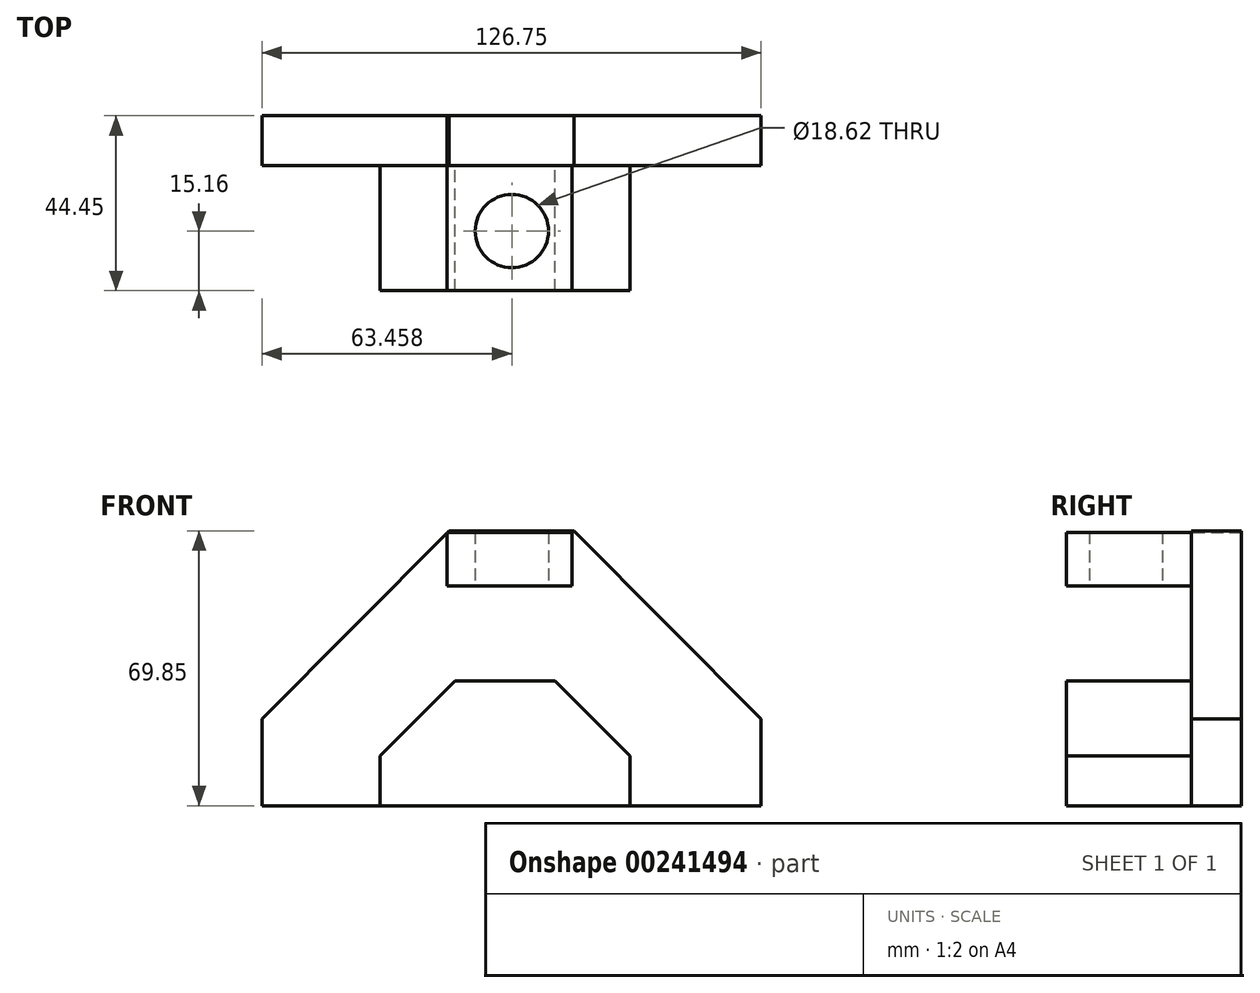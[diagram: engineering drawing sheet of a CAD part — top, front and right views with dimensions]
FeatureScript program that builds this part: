
annotation { "Feature Type Name" : "Feature", "Feature Type Description" : "" }
export const myFeature = defineFeature(function(context is Context, id is Id, definition is map)
    precondition{}
    {
        {
            var Q0;
            Q0=qCreatedBy(makeId("Front.planeOp"),FACE);
            var sketch = newSketch(context, id + "F0", { "sketchPlane" : qUnion([Q0])});
            skLineSegment(sketch, "E0", {"start": v(-11.84, 31.75) * mm, "end": v(13.56, 31.75) * mm});
            skLineSegment(sketch, "E1", {"start": v(-11.84, 31.75) * mm, "end": v(-30.89, 12.7) * mm});
            skLineSegment(sketch, "E2", {"start": v(13.56, 31.75) * mm, "end": v(32.61, 12.7) * mm});
            skLineSegment(sketch, "E3", {"start": v(-30.89, 12.7) * mm, "end": v(-30.89, 0) * mm});
            skLineSegment(sketch, "E4", {"start": v(32.61, 12.7) * mm, "end": v(32.61, 0) * mm});
            skLineSegment(sketch, "E5", {"start": v(-30.89, 0) * mm, "end": v(32.61, 0) * mm});
            skSolve(sketch);
        }
        {
            var Q0;
            Q0=makeQuery(id+"F0.imprint","IMPRINT",FACE,{"disambiguationData":[TD([[makeQuery(id+"F0.imprint","IMPRINT",EDGE,{"derivedFrom":sQuery(id+"F0.wireOp",EDGE,"E0")}),-1.0]])]});
            var Q1;
            Q1=makeQuery(id+"F0.imprint","IMPRINT",FACE,{"disambiguationData":[TD([[makeQuery(id+"F0.imprint","IMPRINT",EDGE,{"derivedFrom":sQuery(id+"F0.wireOp",EDGE,"E0")}),-1.0]])]});
            extrude(context, id + "F1", {"entities" : qUnion([Q0, Q1]), "depth" : 44.45 * mm});
        }
        {
            var Q0;
            Q0=qCreatedBy(makeId("Front.planeOp"),FACE);
            var sketch = newSketch(context, id + "F2", { "sketchPlane" : qUnion([Q0])});
            skLineSegment(sketch, "E6", {"start": v(-13.34, 69.85) * mm, "end": v(18.41, 69.85) * mm});
            skLineSegment(sketch, "E7", {"start": v(-13.34, 69.85) * mm, "end": v(-60.84, 22.1) * mm});
            skLineSegment(sketch, "E8", {"start": v(18.41, 69.85) * mm, "end": v(65.91, 22.1) * mm});
            skLineSegment(sketch, "E9", {"start": v(-60.84, 22.1) * mm, "end": v(-60.84, 0) * mm});
            skLineSegment(sketch, "E10", {"start": v(65.91, 22.1) * mm, "end": v(65.91, 0) * mm});
            skLineSegment(sketch, "E11", {"start": v(-60.84, 0) * mm, "end": v(65.91, 0) * mm});
            skSolve(sketch);
        }
        {
            var Q0;
            Q0 = qSketchRegion(id + "F2", true);
            extrude(context, id + "F3", {"entities" : qUnion([Q0]), "operationType" : NewBodyOperationType.ADD, "depth" : 12.7 * mm});
        }
        {
            var Q0;
            Q0=qCreatedBy(makeId("Front.planeOp"),FACE);
            var sketch = newSketch(context, id + "F4", { "sketchPlane" : qUnion([Q0])});
            skLineSegment(sketch, "E12.bottom", {"start": v(-13.91, 69.47) * mm, "end": v(17.84, 69.47) * mm});
            skLineSegment(sketch, "E12.top", {"start": v(-13.91, 55.86) * mm, "end": v(17.84, 55.86) * mm});
            skLineSegment(sketch, "E12.left", {"start": v(-13.91, 69.47) * mm, "end": v(-13.91, 55.86) * mm});
            skLineSegment(sketch, "E12.right", {"start": v(17.84, 69.47) * mm, "end": v(17.84, 55.86) * mm});
            skSolve(sketch);
        }
        {
            var Q0;
            Q0 = qSketchRegion(id + "F4", true);
            extrude(context, id + "F5", {"entities" : qUnion([Q0]), "operationType" : NewBodyOperationType.ADD, "depth" : 44.45 * mm});
        }
        {
            var Q0;
            Q0=qCreatedBy(makeId("Top.planeOp"),FACE);
            var sketch = newSketch(context, id + "F6", { "sketchPlane" : qUnion([Q0])});
            skCircle(sketch, "E13", {"center": v(2.62, -29.29) * mm, "radius": 9.3 * mm});
            skSolve(sketch);
        }
        {
            var Q0;
            Q0 = qSketchRegion(id + "F6", true);
            extrude(context, id + "F7", {"entities" : qUnion([Q0]), "operationType" : NewBodyOperationType.REMOVE, "depth" : 115.57 * mm, "hasSecondDirection" : true, "secondDirectionOppositeDirection" : false, "secondDirectionDepth" : 54.86 * mm});
        }
    });
